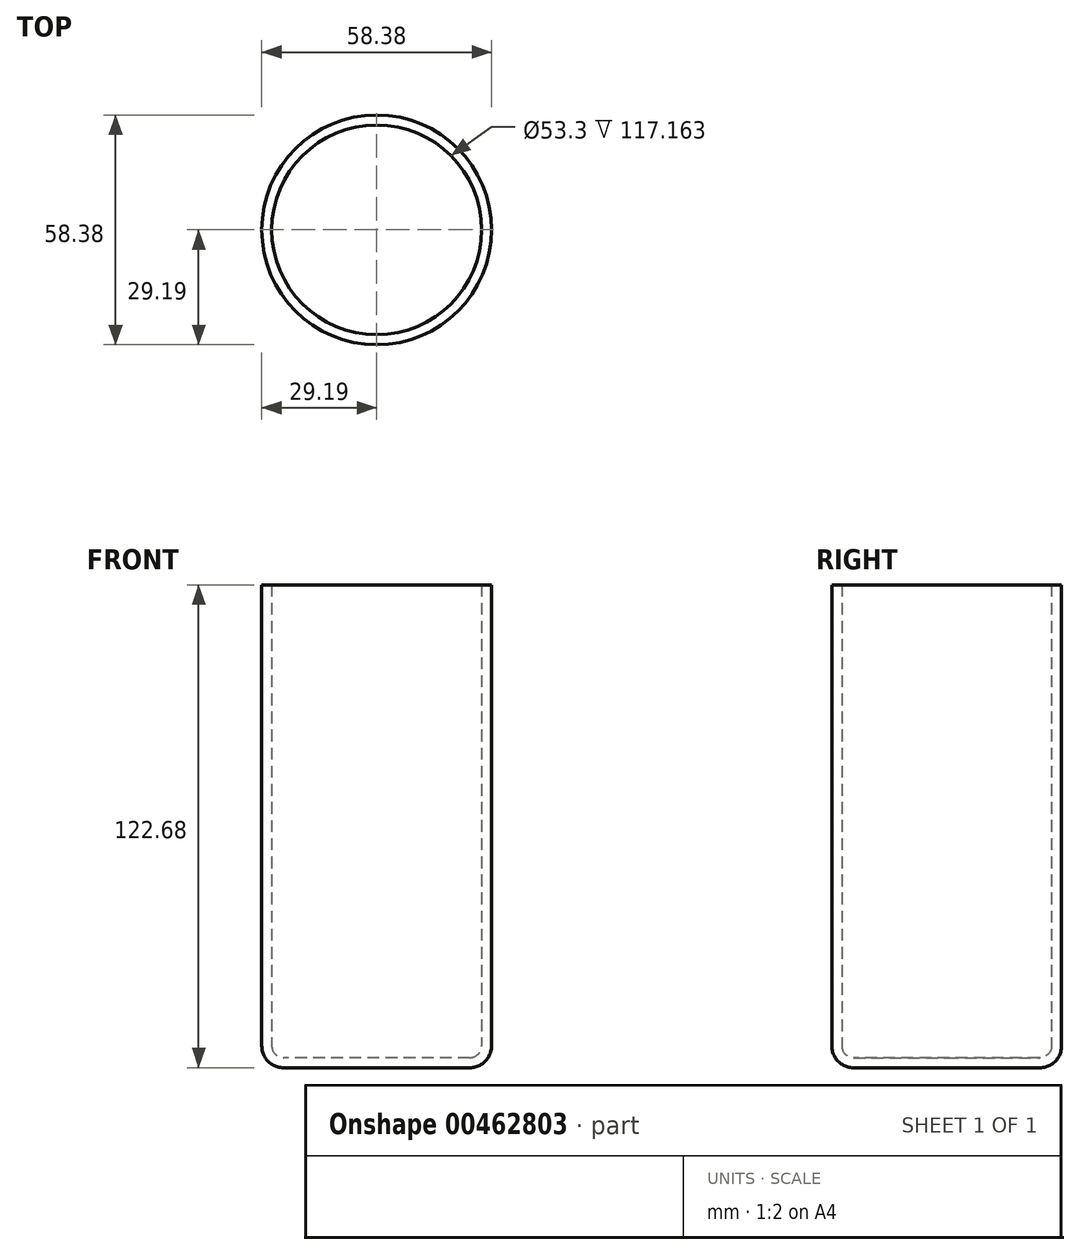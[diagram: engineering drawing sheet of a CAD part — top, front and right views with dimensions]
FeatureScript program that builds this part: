
annotation { "Feature Type Name" : "Feature", "Feature Type Description" : "" }
export const myFeature = defineFeature(function(context is Context, id is Id, definition is map)
    precondition{}
    {
        {
            var Q0;
            Q0=qCreatedBy(makeId("Top.planeOp"),FACE);
            var sketch = newSketch(context, id + "F0", { "sketchPlane" : qUnion([Q0])});
            skCircle(sketch, "E0", {"center": v(0, 0) * mm, "radius": 29.19 * mm});
            skSolve(sketch);
        }
        {
            var Q0;
            Q0=makeQuery(id+"F0.imprint","IMPRINT",FACE,{"disambiguationData":[TD([[makeQuery(id+"F0.imprint","IMPRINT",EDGE,{"derivedFrom":sQuery(id+"F0.wireOp",EDGE,"E0")}),1.0]])]});
            extrude(context, id + "F1", {"entities" : qUnion([Q0]), "depth" : 122.68 * mm, "offsetDistance" : 25.4 * mm});
        }
        {
            var Q0;
            Q0=makeQuery(id+"F1.opExtrude","CAP_FACE",FACE,{"disambiguationData":[OSD([sQuery(id+"F0.wireOp",EDGE,"E0")])],"isStart":true});
            fillet(context, id + "F2", {"entities" : qUnion([Q0]), "radius" : 5.52 * mm, "tangentPropagation" : true, "allowEdgeOverflow" : false});
        }
        {
            var Q0;
            Q0=makeQuery(id+"F1.opExtrude","CAP_FACE",FACE,{"disambiguationData":[OSD([sQuery(id+"F0.wireOp",EDGE,"E0")])],"isStart":false});
            shell(context, id + "F3", {"entities" : qUnion([Q0]), "thickness" : 2.54 * mm});
        }
    });
